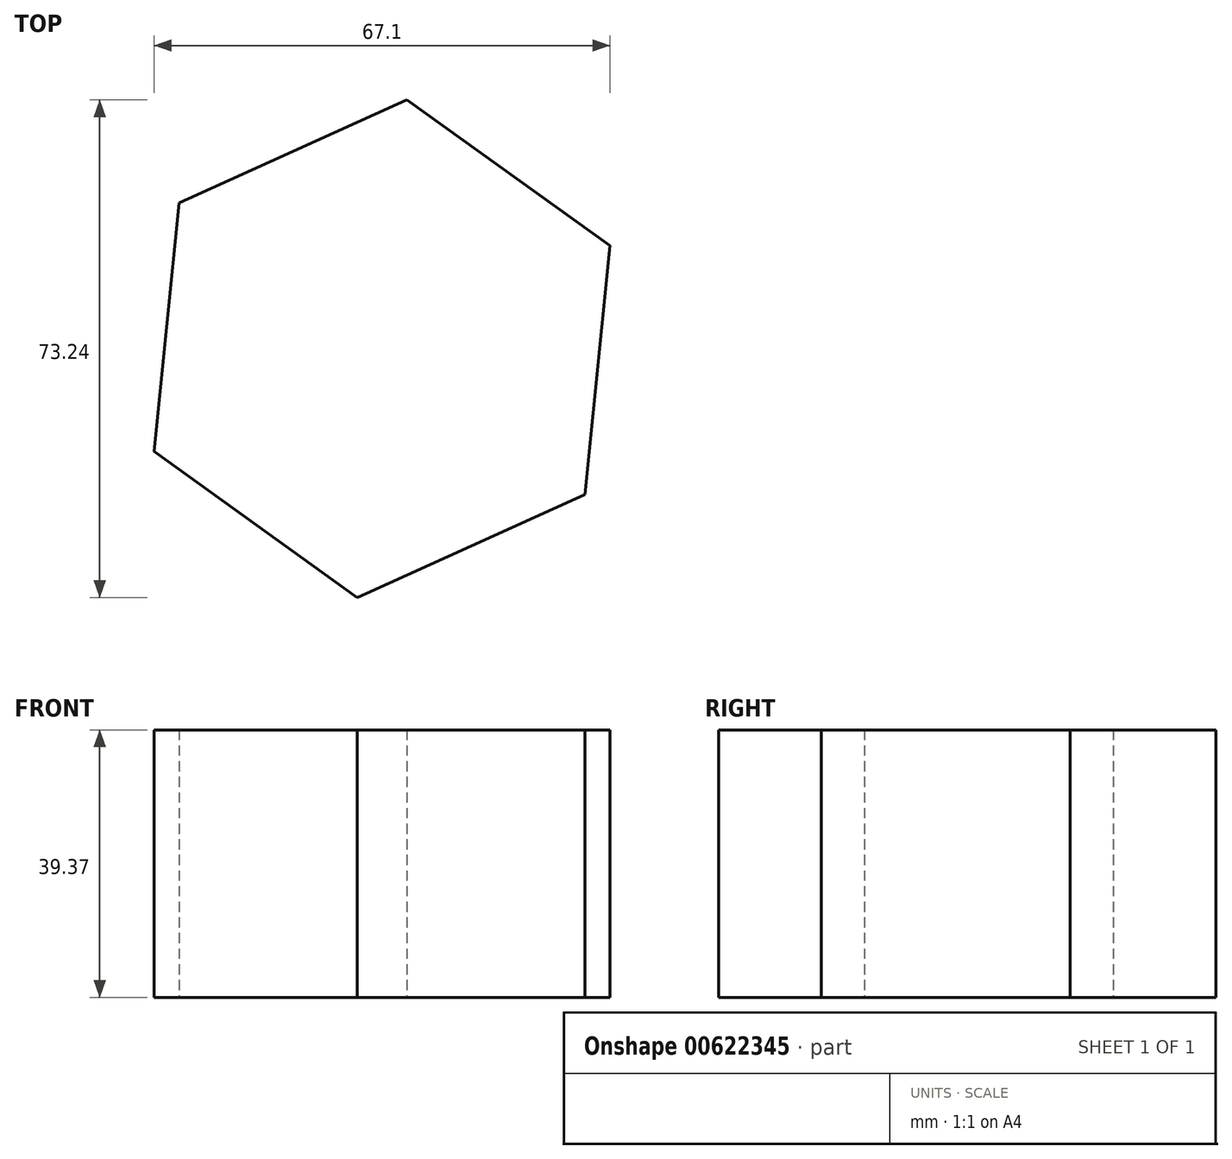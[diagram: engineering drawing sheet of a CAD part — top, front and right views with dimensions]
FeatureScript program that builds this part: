
annotation { "Feature Type Name" : "Feature", "Feature Type Description" : "" }
export const myFeature = defineFeature(function(context is Context, id is Id, definition is map)
    precondition{}
    {
        {
            var Q0;
            Q0=qCreatedBy(makeId("Top.planeOp"),FACE);
            var sketch = newSketch(context, id + "F0", { "sketchPlane" : qUnion([Q0])});
            skCircle(sketch, "E0.cCircle", {"center": v(0, 0) * mm, "radius": 31.87 * mm, "construction": true});
            skLineSegment(sketch, "E0.0", {"start": v(-29.89, 21.48) * mm, "end": v(3.66, 36.62) * mm});
            skLineSegment(sketch, "E0.1", {"start": v(3.66, 36.62) * mm, "end": v(33.55, 15.14) * mm});
            skLineSegment(sketch, "E0.2", {"start": v(33.55, 15.14) * mm, "end": v(29.89, -21.48) * mm});
            skLineSegment(sketch, "E0.3", {"start": v(29.89, -21.48) * mm, "end": v(-3.66, -36.62) * mm});
            skLineSegment(sketch, "E0.4", {"start": v(-3.66, -36.62) * mm, "end": v(-33.55, -15.14) * mm});
            skLineSegment(sketch, "E0.5", {"start": v(-33.55, -15.14) * mm, "end": v(-29.89, 21.48) * mm});
            skPoint(sketch, "E0.0.midPoint", {"position": v(-13.11, 29.05) * mm});
            skSolve(sketch);
        }
        {
            var Q0;
            Q0=makeQuery(id+"F0.imprint","IMPRINT",FACE,{"disambiguationData":[TD([[makeQuery(id+"F0.imprint","IMPRINT",EDGE,{"derivedFrom":sQuery(id+"F0.wireOp",EDGE,"E0.0")}),-1.0]])]});
            extrude(context, id + "F1", {"entities" : qUnion([Q0]), "depth" : 39.37 * mm, "offsetDistance" : 25.4 * mm});
        }
    });
